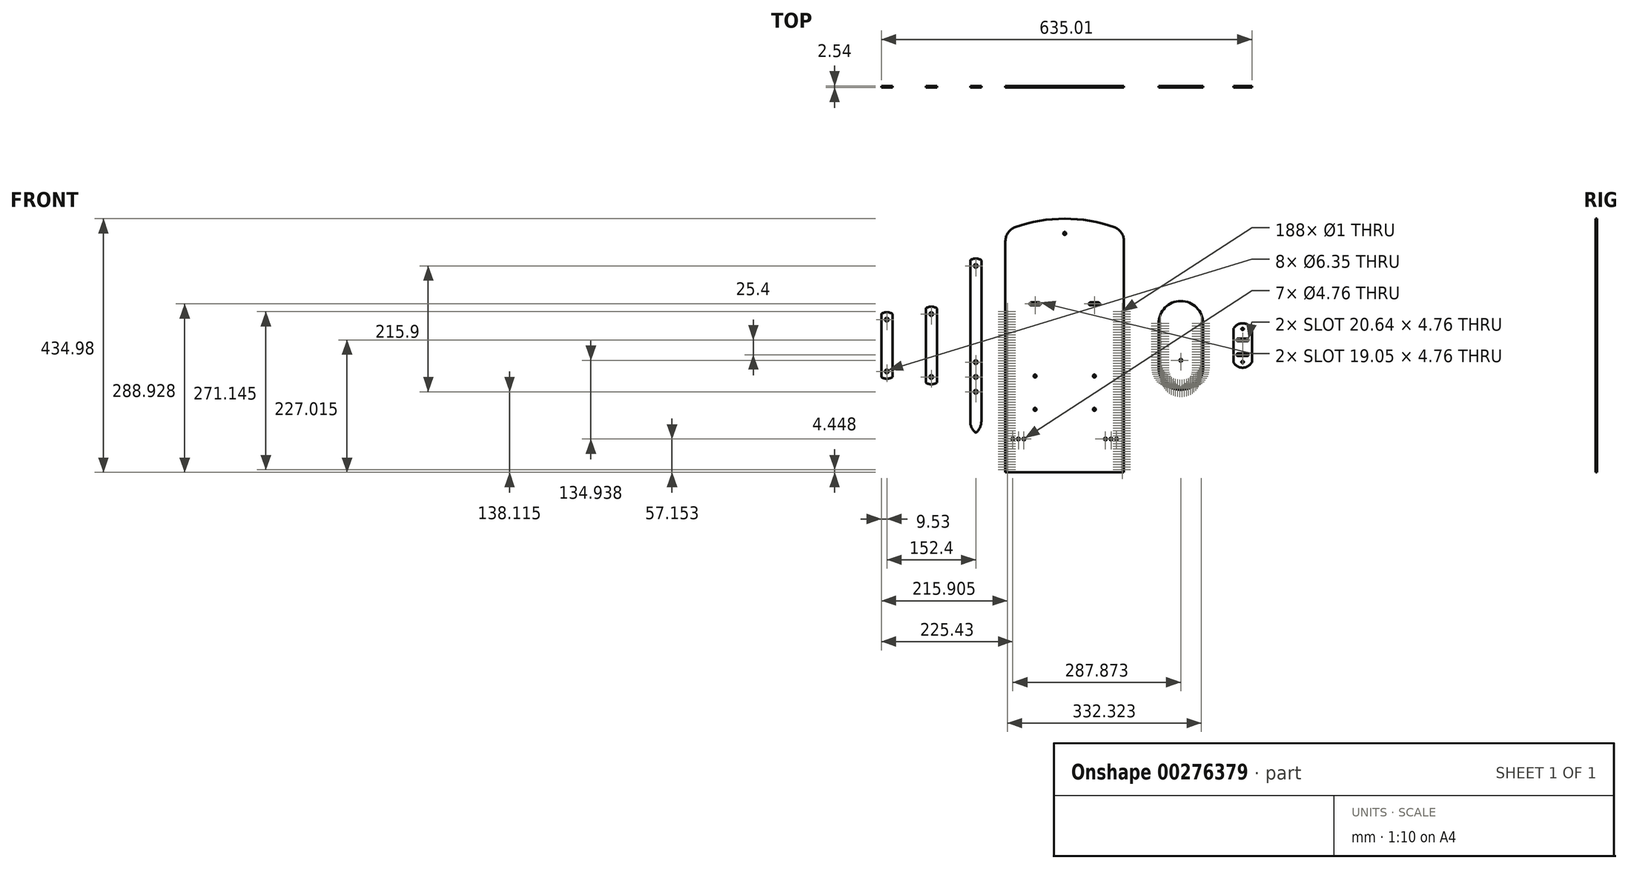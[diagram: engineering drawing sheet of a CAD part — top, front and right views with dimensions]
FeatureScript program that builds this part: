
annotation { "Feature Type Name" : "Feature", "Feature Type Description" : "" }
export const myFeature = defineFeature(function(context is Context, id is Id, definition is map)
    precondition{}
    {
        {
            var Q0;
            Q0=qCreatedBy(makeId("Front.planeOp"),FACE);
            var sketch = newSketch(context, id + "F0", { "sketchPlane" : qUnion([Q0])});
            skLineSegment(sketch, "E0.bottom", {"start": v(101.6, -217.49) * mm, "end": v(-101.6, -217.49) * mm, "construction": true});
            skLineSegment(sketch, "E0.top", {"start": v(101.6, 217.49) * mm, "end": v(-101.6, 217.49) * mm, "construction": true});
            skLineSegment(sketch, "E0.left", {"start": v(101.6, -217.49) * mm, "end": v(101.6, 217.49) * mm, "construction": true});
            skLineSegment(sketch, "E0.right", {"start": v(-101.6, -217.49) * mm, "end": v(-101.6, 217.49) * mm, "construction": true});
            skPoint(sketch, "E0.middle", {"position": v(0, 0) * mm});
            skArc(sketch, "E1", {"start": v(84.67, 202.96) * mm, "mid": v(0, 217.49) * mm, "end": v(-84.67, 202.96) * mm});
            skLineSegment(sketch, "E2", {"start": v(0, 0) * mm, "end": v(0, 217.49) * mm, "construction": true});
            skArc(sketch, "E3", {"start": v(-84.67, 202.96) * mm, "mid": v(-96.94, 193.68) * mm, "end": v(-101.6, 179.01) * mm});
            skPoint(sketch, "E4.orphan", {"position": v(-101.6, 196.28) * mm});
            skArc(sketch, "E5.MirrorCS", {"start": v(84.67, 202.96) * mm, "mid": v(96.94, 193.68) * mm, "end": v(101.6, 179.01) * mm});
            skPoint(sketch, "E6.orphan", {"position": v(101.6, 196.28) * mm});
            skLineSegment(sketch, "E7", {"start": v(-101.6, 179.01) * mm, "end": v(-101.6, -217.49) * mm});
            skLineSegment(sketch, "E8", {"start": v(101.6, -217.49) * mm, "end": v(-101.6, -217.49) * mm});
            skLineSegment(sketch, "E9", {"start": v(101.6, -217.49) * mm, "end": v(101.6, 179.01) * mm});
            skCircle(sketch, "E10", {"center": v(0, 192.09) * mm, "radius": 2.5 * mm});
            skLineSegment(sketch, "E11.bottom", {"start": v(-57.94, 69.06) * mm, "end": v(-43.66, 69.06) * mm});
            skLineSegment(sketch, "E11.top", {"start": v(-57.94, 73.82) * mm, "end": v(-43.66, 73.82) * mm});
            skLineSegment(sketch, "E11.left", {"start": v(-57.94, 69.06) * mm, "end": v(-57.94, 73.82) * mm, "construction": true});
            skLineSegment(sketch, "E11.right", {"start": v(-43.66, 69.06) * mm, "end": v(-43.66, 73.82) * mm, "construction": true});
            skPoint(sketch, "E11.middle", {"position": v(-50.8, 71.44) * mm});
            skArc(sketch, "E12", {"start": v(-43.66, 69.06) * mm, "mid": v(-41.27, 71.44) * mm, "end": v(-43.66, 73.82) * mm});
            skArc(sketch, "E13", {"start": v(-57.94, 73.82) * mm, "mid": v(-60.32, 71.44) * mm, "end": v(-57.94, 69.06) * mm});
            skLineSegment(sketch, "E14.MirrorCS", {"start": v(57.94, 73.82) * mm, "end": v(43.66, 73.82) * mm});
            skArc(sketch, "E15.MirrorCS", {"start": v(57.94, 73.82) * mm, "mid": v(60.32, 71.44) * mm, "end": v(57.94, 69.06) * mm});
            skLineSegment(sketch, "E16.MirrorCS", {"start": v(57.94, 69.06) * mm, "end": v(43.66, 69.06) * mm});
            skArc(sketch, "E17.MirrorCS", {"start": v(43.66, 69.06) * mm, "mid": v(41.27, 71.44) * mm, "end": v(43.66, 73.82) * mm});
            skLineSegment(sketch, "E18", {"start": v(-50.8, 71.44) * mm, "end": v(-50.8, -52.39) * mm, "construction": true});
            skCircle(sketch, "E19", {"center": v(-50.8, -52.39) * mm, "radius": 2.5 * mm});
            skCircle(sketch, "E20", {"center": v(-50.8, -109.54) * mm, "radius": 2.5 * mm});
            skCircle(sketch, "E21.MirrorC", {"center": v(50.8, -52.39) * mm, "radius": 2.5 * mm});
            skCircle(sketch, "E22.MirrorC", {"center": v(50.8, -109.54) * mm, "radius": 2.5 * mm});
            skLineSegment(sketch, "E23", {"start": v(-101.6, -160.34) * mm, "end": v(-57.15, -160.34) * mm, "construction": true});
            skCircle(sketch, "E24", {"center": v(-88.9, -160.34) * mm, "radius": 2.38 * mm});
            skCircle(sketch, "E25", {"center": v(-79.37, -160.34) * mm, "radius": 2.38 * mm});
            skCircle(sketch, "E26", {"center": v(-69.85, -160.34) * mm, "radius": 2.38 * mm});
            skCircle(sketch, "E27.MirrorC", {"center": v(88.9, -160.34) * mm, "radius": 2.38 * mm});
            skCircle(sketch, "E28.MirrorC", {"center": v(79.37, -160.34) * mm, "radius": 2.38 * mm});
            skCircle(sketch, "E29.MirrorC", {"center": v(69.85, -160.34) * mm, "radius": 2.38 * mm});
            skSolve(sketch);
        }
        {
            var Q0;
            Q0 = qSketchRegion(id + "F0", true);
            extrude(context, id + "F1", {"entities" : qUnion([Q0]), "depth" : 2.54 * mm});
        }
        {
            var Q0;
            Q0=qCreatedBy(makeId("Front.planeOp"),FACE);
            var sketch = newSketch(context, id + "F2", { "sketchPlane" : qUnion([Q0])});
            skLineSegment(sketch, "E30.bottom", {"start": v(237.07, -38.1) * mm, "end": v(160.87, -38.1) * mm, "construction": true});
            skLineSegment(sketch, "E30.top", {"start": v(237.07, 38.1) * mm, "end": v(160.87, 38.1) * mm, "construction": true});
            skLineSegment(sketch, "E30.left", {"start": v(237.07, -38.1) * mm, "end": v(237.07, 38.1) * mm});
            skLineSegment(sketch, "E30.right", {"start": v(160.87, -38.1) * mm, "end": v(160.87, 38.1) * mm});
            skPoint(sketch, "E30.middle", {"position": v(198.97, 0) * mm});
            skArc(sketch, "E31", {"start": v(237.07, 38.1) * mm, "mid": v(198.97, 76.2) * mm, "end": v(160.87, 38.1) * mm});
            skArc(sketch, "E32", {"start": v(160.87, -38.1) * mm, "mid": v(198.97, -76.2) * mm, "end": v(237.07, -38.1) * mm});
            skCircle(sketch, "E33", {"center": v(198.97, -25.4) * mm, "radius": 2.38 * mm});
            skSolve(sketch);
        }
        {
            var Q0;
            Q0 = qSketchRegion(id + "F2", true);
            extrude(context, id + "F3", {"entities" : qUnion([Q0]), "depth" : 2.54 * mm});
        }
        {
            var Q0;
            Q0=makeQuery(id+"F3.opExtrude","CAP_FACE",FACE,{"disambiguationData":[OSD([sQuery(id+"F2.wireOp",EDGE,"E30.left"),sQuery(id+"F2.wireOp",EDGE,"E30.right"),sQuery(id+"F2.wireOp",EDGE,"E31"),sQuery(id+"F2.wireOp",EDGE,"E32"),sQuery(id+"F2.wireOp",EDGE,"E33")])],"isStart":false});
            var sketch = newSketch(context, id + "F4", { "sketchPlane" : qUnion([Q0])});
            skArc(sketch, "E34.0", {"start": v(233.9, 38.1) * mm, "mid": v(198.97, 73.02) * mm, "end": v(164.05, 38.1) * mm, "construction": true});
            skLineSegment(sketch, "E34.1", {"start": v(233.9, -38.1) * mm, "end": v(233.9, 38.1) * mm, "construction": true});
            skArc(sketch, "E34.2", {"start": v(164.05, -38.1) * mm, "mid": v(198.97, -73.02) * mm, "end": v(233.9, -38.1) * mm, "construction": true});
            skLineSegment(sketch, "E34.3", {"start": v(164.05, -38.1) * mm, "end": v(164.05, 38.1) * mm, "construction": true});
            skCircle(sketch, "E35", {"center": v(233.9, 38.1) * mm, "radius": 0.5 * mm});
            skCircle(sketch, "E36.0.1.0", {"center": v(233.9, 33.62) * mm, "radius": 0.5 * mm});
            skCircle(sketch, "E36.0.2.0", {"center": v(233.9, 29.14) * mm, "radius": 0.5 * mm});
            skCircle(sketch, "E36.0.3.0", {"center": v(233.9, 24.65) * mm, "radius": 0.5 * mm});
            skCircle(sketch, "E36.0.4.0", {"center": v(233.9, 20.17) * mm, "radius": 0.5 * mm});
            skCircle(sketch, "E36.0.5.0", {"center": v(233.9, 15.69) * mm, "radius": 0.5 * mm});
            skCircle(sketch, "E36.0.6.0", {"center": v(233.9, 11.2) * mm, "radius": 0.5 * mm});
            skCircle(sketch, "E36.0.7.0", {"center": v(233.9, 6.72) * mm, "radius": 0.5 * mm});
            skCircle(sketch, "E36.0.8.0", {"center": v(233.9, 2.24) * mm, "radius": 0.5 * mm});
            skCircle(sketch, "E36.0.9.0", {"center": v(233.9, -2.24) * mm, "radius": 0.5 * mm});
            skCircle(sketch, "E36.0.10.0", {"center": v(233.9, -6.72) * mm, "radius": 0.5 * mm});
            skCircle(sketch, "E36.0.11.0", {"center": v(233.9, -11.2) * mm, "radius": 0.5 * mm});
            skCircle(sketch, "E36.0.12.0", {"center": v(233.9, -15.69) * mm, "radius": 0.5 * mm});
            skCircle(sketch, "E36.0.13.0", {"center": v(233.9, -20.17) * mm, "radius": 0.5 * mm});
            skCircle(sketch, "E36.0.14.0", {"center": v(233.9, -24.65) * mm, "radius": 0.5 * mm});
            skCircle(sketch, "E36.0.15.0", {"center": v(233.9, -29.14) * mm, "radius": 0.5 * mm});
            skCircle(sketch, "E36.0.16.0", {"center": v(233.9, -33.62) * mm, "radius": 0.5 * mm});
            skCircle(sketch, "E36.0.17.0", {"center": v(233.9, -38.1) * mm, "radius": 0.5 * mm});
            skLineSegment(sketch, "E36.direction1", {"start": v(233.9, 38.1) * mm, "end": v(259.3, 38.1) * mm, "construction": true});
            skLineSegment(sketch, "E36.direction2", {"start": v(233.9, 38.1) * mm, "end": v(233.9, 33.62) * mm, "construction": true});
            skCircle(sketch, "E37.1.0", {"center": v(233.7, -41.88) * mm, "radius": 0.5 * mm});
            skCircle(sketch, "E37.2.0", {"center": v(233.08, -45.6) * mm, "radius": 0.5 * mm});
            skCircle(sketch, "E37.3.0", {"center": v(232.07, -49.25) * mm, "radius": 0.5 * mm});
            skCircle(sketch, "E37.4.0", {"center": v(230.67, -52.76) * mm, "radius": 0.5 * mm});
            skCircle(sketch, "E37.5.0", {"center": v(228.9, -56.1) * mm, "radius": 0.5 * mm});
            skCircle(sketch, "E37.6.0", {"center": v(226.78, -59.24) * mm, "radius": 0.5 * mm});
            skCircle(sketch, "E37.7.0", {"center": v(224.33, -62.12) * mm, "radius": 0.5 * mm});
            skCircle(sketch, "E37.8.0", {"center": v(221.58, -64.72) * mm, "radius": 0.5 * mm});
            skCircle(sketch, "E37.9.0", {"center": v(218.57, -67) * mm, "radius": 0.5 * mm});
            skCircle(sketch, "E37.10.0", {"center": v(215.33, -68.96) * mm, "radius": 0.5 * mm});
            skCircle(sketch, "E37.11.0", {"center": v(211.9, -70.54) * mm, "radius": 0.5 * mm});
            skCircle(sketch, "E37.12.0", {"center": v(208.32, -71.75) * mm, "radius": 0.5 * mm});
            skCircle(sketch, "E37.13.0", {"center": v(204.62, -72.56) * mm, "radius": 0.5 * mm});
            skCircle(sketch, "E37.14.0", {"center": v(200.86, -72.97) * mm, "radius": 0.5 * mm});
            skCircle(sketch, "E37.15.0", {"center": v(197.08, -72.97) * mm, "radius": 0.5 * mm});
            skCircle(sketch, "E37.16.0", {"center": v(193.32, -72.56) * mm, "radius": 0.5 * mm});
            skCircle(sketch, "E37.17.0", {"center": v(189.63, -71.75) * mm, "radius": 0.5 * mm});
            skCircle(sketch, "E37.18.0", {"center": v(186.05, -70.54) * mm, "radius": 0.5 * mm});
            skCircle(sketch, "E37.19.0", {"center": v(182.61, -68.96) * mm, "radius": 0.5 * mm});
            skCircle(sketch, "E37.20.0", {"center": v(179.37, -67) * mm, "radius": 0.5 * mm});
            skCircle(sketch, "E37.21.0", {"center": v(176.36, -64.72) * mm, "radius": 0.5 * mm});
            skCircle(sketch, "E37.22.0", {"center": v(173.62, -62.12) * mm, "radius": 0.5 * mm});
            skCircle(sketch, "E37.23.0", {"center": v(171.17, -59.24) * mm, "radius": 0.5 * mm});
            skCircle(sketch, "E37.24.0", {"center": v(169.05, -56.1) * mm, "radius": 0.5 * mm});
            skCircle(sketch, "E37.25.0", {"center": v(167.28, -52.76) * mm, "radius": 0.5 * mm});
            skCircle(sketch, "E37.26.0", {"center": v(165.88, -49.25) * mm, "radius": 0.5 * mm});
            skCircle(sketch, "E37.27.0", {"center": v(164.86, -45.6) * mm, "radius": 0.5 * mm});
            skCircle(sketch, "E37.28.0", {"center": v(164.25, -41.88) * mm, "radius": 0.5 * mm});
            skCircle(sketch, "E37.29.0", {"center": v(164.05, -38.1) * mm, "radius": 0.5 * mm});
            skLineSegment(sketch, "E37.anchor1", {"start": v(198.97, -38.1) * mm, "end": v(233.9, -38.1) * mm, "construction": true});
            skLineSegment(sketch, "E37.anchor2", {"start": v(198.97, -38.1) * mm, "end": v(164.05, -38.1) * mm, "construction": true});
            skLineSegment(sketch, "E38", {"start": v(198.97, 38.1) * mm, "end": v(198.97, -38.1) * mm, "construction": true});
            skCircle(sketch, "E39.MirrorC", {"center": v(164.05, 38.1) * mm, "radius": 0.5 * mm});
            skCircle(sketch, "E40.MirrorC", {"center": v(164.05, 33.62) * mm, "radius": 0.5 * mm});
            skCircle(sketch, "E41.MirrorC", {"center": v(164.05, -20.17) * mm, "radius": 0.5 * mm});
            skCircle(sketch, "E42.MirrorC", {"center": v(164.05, -24.65) * mm, "radius": 0.5 * mm});
            skCircle(sketch, "E43.MirrorC", {"center": v(164.05, -29.14) * mm, "radius": 0.5 * mm});
            skCircle(sketch, "E44.MirrorC", {"center": v(164.05, -2.24) * mm, "radius": 0.5 * mm});
            skCircle(sketch, "E45.MirrorC", {"center": v(164.05, -6.72) * mm, "radius": 0.5 * mm});
            skCircle(sketch, "E46.MirrorC", {"center": v(164.05, -11.2) * mm, "radius": 0.5 * mm});
            skCircle(sketch, "E47.MirrorC", {"center": v(164.05, -15.69) * mm, "radius": 0.5 * mm});
            skCircle(sketch, "E48.MirrorC", {"center": v(164.05, 29.14) * mm, "radius": 0.5 * mm});
            skLineSegment(sketch, "E49.MirrorCS", {"start": v(164.05, 38.1) * mm, "end": v(164.05, 33.62) * mm, "construction": true});
            skCircle(sketch, "E50.MirrorC", {"center": v(164.05, 24.65) * mm, "radius": 0.5 * mm});
            skCircle(sketch, "E51.MirrorC", {"center": v(164.05, 11.2) * mm, "radius": 0.5 * mm});
            skCircle(sketch, "E52.MirrorC", {"center": v(164.05, -33.62) * mm, "radius": 0.5 * mm});
            skCircle(sketch, "E53.MirrorC", {"center": v(164.05, 6.72) * mm, "radius": 0.5 * mm});
            skCircle(sketch, "E54.MirrorC", {"center": v(164.05, 2.24) * mm, "radius": 0.5 * mm});
            skCircle(sketch, "E55.MirrorC", {"center": v(164.05, 20.17) * mm, "radius": 0.5 * mm});
            skCircle(sketch, "E56.MirrorC", {"center": v(164.05, 15.69) * mm, "radius": 0.5 * mm});
            skSolve(sketch);
        }
        {
            var Q0;
            Q0 = qSketchRegion(id + "F4", true);
            extrude(context, id + "F5", {"entities" : qUnion([Q0]), "operationType" : NewBodyOperationType.REMOVE, "endBound" : BoundingType.THROUGH_ALL, "oppositeDirection" : true, "depth" : 25.4 * mm});
        }
        {
            var Q0;
            Q0=makeQuery(id+"F1.opExtrude","CAP_FACE",FACE,{"disambiguationData":[OSD([sQuery(id+"F0.wireOp",EDGE,"E1"),sQuery(id+"F0.wireOp",EDGE,"E3"),sQuery(id+"F0.wireOp",EDGE,"E5.MirrorCS"),sQuery(id+"F0.wireOp",EDGE,"E7"),sQuery(id+"F0.wireOp",EDGE,"E8"),sQuery(id+"F0.wireOp",EDGE,"E9"),sQuery(id+"F0.wireOp",EDGE,"E10"),sQuery(id+"F0.wireOp",EDGE,"E11.bottom"),sQuery(id+"F0.wireOp",EDGE,"E11.top"),sQuery(id+"F0.wireOp",EDGE,"E12"),sQuery(id+"F0.wireOp",EDGE,"E13"),sQuery(id+"F0.wireOp",EDGE,"E14.MirrorCS"),sQuery(id+"F0.wireOp",EDGE,"E15.MirrorCS"),sQuery(id+"F0.wireOp",EDGE,"E16.MirrorCS"),sQuery(id+"F0.wireOp",EDGE,"E17.MirrorCS"),sQuery(id+"F0.wireOp",EDGE,"E19"),sQuery(id+"F0.wireOp",EDGE,"E20"),sQuery(id+"F0.wireOp",EDGE,"E21.MirrorC"),sQuery(id+"F0.wireOp",EDGE,"E22.MirrorC"),sQuery(id+"F0.wireOp",EDGE,"E24"),sQuery(id+"F0.wireOp",EDGE,"E25"),sQuery(id+"F0.wireOp",EDGE,"E26"),sQuery(id+"F0.wireOp",EDGE,"E27.MirrorC"),sQuery(id+"F0.wireOp",EDGE,"E28.MirrorC"),sQuery(id+"F0.wireOp",EDGE,"E29.MirrorC")])],"isStart":false});
            var sketch = newSketch(context, id + "F6", { "sketchPlane" : qUnion([Q0])});
            skLineSegment(sketch, "E57", {"start": v(98.43, -83.45) * mm, "end": v(98.43, -217.49) * mm, "construction": true});
            skCircle(sketch, "E58", {"center": v(98.43, -213.04) * mm, "radius": 0.5 * mm});
            skCircle(sketch, "E59.0.1.0", {"center": v(98.43, -208.6) * mm, "radius": 0.5 * mm});
            skCircle(sketch, "E59.0.2.0", {"center": v(98.43, -204.15) * mm, "radius": 0.5 * mm});
            skCircle(sketch, "E59.0.3.0", {"center": v(98.43, -199.7) * mm, "radius": 0.5 * mm});
            skCircle(sketch, "E59.0.4.0", {"center": v(98.43, -195.26) * mm, "radius": 0.5 * mm});
            skCircle(sketch, "E59.0.5.0", {"center": v(98.43, -190.82) * mm, "radius": 0.5 * mm});
            skCircle(sketch, "E59.0.6.0", {"center": v(98.43, -186.37) * mm, "radius": 0.5 * mm});
            skCircle(sketch, "E59.0.7.0", {"center": v(98.43, -181.93) * mm, "radius": 0.5 * mm});
            skCircle(sketch, "E59.0.8.0", {"center": v(98.43, -177.48) * mm, "radius": 0.5 * mm});
            skCircle(sketch, "E59.0.9.0", {"center": v(98.43, -173.04) * mm, "radius": 0.5 * mm});
            skCircle(sketch, "E59.0.10.0", {"center": v(98.43, -168.6) * mm, "radius": 0.5 * mm});
            skCircle(sketch, "E59.0.11.0", {"center": v(98.43, -164.15) * mm, "radius": 0.5 * mm});
            skCircle(sketch, "E59.0.12.0", {"center": v(98.43, -159.7) * mm, "radius": 0.5 * mm});
            skCircle(sketch, "E59.0.13.0", {"center": v(98.43, -155.26) * mm, "radius": 0.5 * mm});
            skCircle(sketch, "E59.0.14.0", {"center": v(98.43, -150.81) * mm, "radius": 0.5 * mm});
            skCircle(sketch, "E59.0.15.0", {"center": v(98.43, -146.37) * mm, "radius": 0.5 * mm});
            skCircle(sketch, "E59.0.16.0", {"center": v(98.43, -141.92) * mm, "radius": 0.5 * mm});
            skCircle(sketch, "E59.0.17.0", {"center": v(98.43, -137.48) * mm, "radius": 0.5 * mm});
            skCircle(sketch, "E59.0.18.0", {"center": v(98.43, -133.03) * mm, "radius": 0.5 * mm});
            skCircle(sketch, "E59.0.19.0", {"center": v(98.43, -128.59) * mm, "radius": 0.5 * mm});
            skCircle(sketch, "E59.0.20.0", {"center": v(98.43, -124.14) * mm, "radius": 0.5 * mm});
            skCircle(sketch, "E59.0.21.0", {"center": v(98.43, -119.7) * mm, "radius": 0.5 * mm});
            skCircle(sketch, "E59.0.22.0", {"center": v(98.43, -115.25) * mm, "radius": 0.5 * mm});
            skCircle(sketch, "E59.0.23.0", {"center": v(98.43, -110.8) * mm, "radius": 0.5 * mm});
            skCircle(sketch, "E59.0.24.0", {"center": v(98.43, -106.36) * mm, "radius": 0.5 * mm});
            skCircle(sketch, "E59.0.25.0", {"center": v(98.43, -101.92) * mm, "radius": 0.5 * mm});
            skCircle(sketch, "E59.0.26.0", {"center": v(98.43, -97.47) * mm, "radius": 0.5 * mm});
            skCircle(sketch, "E59.0.27.0", {"center": v(98.43, -93.03) * mm, "radius": 0.5 * mm});
            skCircle(sketch, "E59.0.28.0", {"center": v(98.43, -88.58) * mm, "radius": 0.5 * mm});
            skCircle(sketch, "E59.0.29.0", {"center": v(98.43, -84.14) * mm, "radius": 0.5 * mm});
            skCircle(sketch, "E59.0.30.0", {"center": v(98.43, -79.7) * mm, "radius": 0.5 * mm});
            skCircle(sketch, "E59.0.31.0", {"center": v(98.43, -75.25) * mm, "radius": 0.5 * mm});
            skCircle(sketch, "E59.0.32.0", {"center": v(98.43, -70.8) * mm, "radius": 0.5 * mm});
            skCircle(sketch, "E59.0.33.0", {"center": v(98.43, -66.36) * mm, "radius": 0.5 * mm});
            skCircle(sketch, "E59.0.34.0", {"center": v(98.43, -61.91) * mm, "radius": 0.5 * mm});
            skCircle(sketch, "E59.0.35.0", {"center": v(98.43, -57.47) * mm, "radius": 0.5 * mm});
            skCircle(sketch, "E59.0.36.0", {"center": v(98.43, -53.02) * mm, "radius": 0.5 * mm});
            skCircle(sketch, "E59.0.37.0", {"center": v(98.43, -48.58) * mm, "radius": 0.5 * mm});
            skCircle(sketch, "E59.0.38.0", {"center": v(98.43, -44.13) * mm, "radius": 0.5 * mm});
            skCircle(sketch, "E59.0.39.0", {"center": v(98.43, -39.69) * mm, "radius": 0.5 * mm});
            skCircle(sketch, "E59.0.40.0", {"center": v(98.43, -35.24) * mm, "radius": 0.5 * mm});
            skCircle(sketch, "E59.0.41.0", {"center": v(98.43, -30.8) * mm, "radius": 0.5 * mm});
            skCircle(sketch, "E59.0.42.0", {"center": v(98.43, -26.35) * mm, "radius": 0.5 * mm});
            skCircle(sketch, "E59.0.43.0", {"center": v(98.43, -21.9) * mm, "radius": 0.5 * mm});
            skCircle(sketch, "E59.0.44.0", {"center": v(98.43, -17.46) * mm, "radius": 0.5 * mm});
            skCircle(sketch, "E59.0.45.0", {"center": v(98.43, -13.02) * mm, "radius": 0.5 * mm});
            skCircle(sketch, "E59.0.46.0", {"center": v(98.43, -8.57) * mm, "radius": 0.5 * mm});
            skCircle(sketch, "E59.0.47.0", {"center": v(98.43, -4.13) * mm, "radius": 0.5 * mm});
            skCircle(sketch, "E59.0.48.0", {"center": v(98.43, 0.32) * mm, "radius": 0.5 * mm});
            skCircle(sketch, "E59.0.49.0", {"center": v(98.43, 4.76) * mm, "radius": 0.5 * mm});
            skCircle(sketch, "E59.0.50.0", {"center": v(98.43, 9.2) * mm, "radius": 0.5 * mm});
            skCircle(sketch, "E59.0.51.0", {"center": v(98.43, 13.65) * mm, "radius": 0.5 * mm});
            skCircle(sketch, "E59.0.52.0", {"center": v(98.43, 18.1) * mm, "radius": 0.5 * mm});
            skCircle(sketch, "E59.0.53.0", {"center": v(98.43, 22.54) * mm, "radius": 0.5 * mm});
            skCircle(sketch, "E59.0.54.0", {"center": v(98.43, 26.99) * mm, "radius": 0.5 * mm});
            skCircle(sketch, "E59.0.55.0", {"center": v(98.43, 31.43) * mm, "radius": 0.5 * mm});
            skCircle(sketch, "E59.0.56.0", {"center": v(98.43, 35.88) * mm, "radius": 0.5 * mm});
            skCircle(sketch, "E59.0.57.0", {"center": v(98.43, 40.32) * mm, "radius": 0.5 * mm});
            skCircle(sketch, "E59.0.58.0", {"center": v(98.43, 44.77) * mm, "radius": 0.5 * mm});
            skCircle(sketch, "E59.0.59.0", {"center": v(98.43, 49.21) * mm, "radius": 0.5 * mm});
            skCircle(sketch, "E59.0.60.0", {"center": v(98.43, 53.66) * mm, "radius": 0.5 * mm});
            skCircle(sketch, "E59.0.61.0", {"center": v(98.43, 58.1) * mm, "radius": 0.5 * mm});
            skLineSegment(sketch, "E59.direction1", {"start": v(98.43, -213.04) * mm, "end": v(123.83, -213.04) * mm, "construction": true});
            skLineSegment(sketch, "E59.direction2", {"start": v(98.43, -213.04) * mm, "end": v(98.43, -208.6) * mm, "construction": true});
            skCircle(sketch, "E60.MirrorC", {"center": v(-98.43, -213.04) * mm, "radius": 0.5 * mm});
            skLineSegment(sketch, "E61.MirrorCS", {"start": v(-98.43, -213.04) * mm, "end": v(-98.43, -208.6) * mm, "construction": true});
            skCircle(sketch, "E62.MirrorC", {"center": v(-98.43, -204.15) * mm, "radius": 0.5 * mm});
            skCircle(sketch, "E63.MirrorC", {"center": v(-98.43, -208.6) * mm, "radius": 0.5 * mm});
            skCircle(sketch, "E64.MirrorC", {"center": v(-98.43, -164.15) * mm, "radius": 0.5 * mm});
            skCircle(sketch, "E65.MirrorC", {"center": v(-98.43, -168.6) * mm, "radius": 0.5 * mm});
            skCircle(sketch, "E66.MirrorC", {"center": v(-98.43, -173.04) * mm, "radius": 0.5 * mm});
            skCircle(sketch, "E67.MirrorC", {"center": v(-98.43, -177.48) * mm, "radius": 0.5 * mm});
            skCircle(sketch, "E68.MirrorC", {"center": v(-98.43, -181.93) * mm, "radius": 0.5 * mm});
            skCircle(sketch, "E69.MirrorC", {"center": v(-98.43, -186.37) * mm, "radius": 0.5 * mm});
            skCircle(sketch, "E70.MirrorC", {"center": v(-98.43, -190.82) * mm, "radius": 0.5 * mm});
            skCircle(sketch, "E71.MirrorC", {"center": v(-98.43, -195.26) * mm, "radius": 0.5 * mm});
            skCircle(sketch, "E72.MirrorC", {"center": v(-98.43, -199.7) * mm, "radius": 0.5 * mm});
            skCircle(sketch, "E73.MirrorC", {"center": v(-98.43, -159.7) * mm, "radius": 0.5 * mm});
            skCircle(sketch, "E74.MirrorC", {"center": v(-98.43, -79.7) * mm, "radius": 0.5 * mm});
            skCircle(sketch, "E75.MirrorC", {"center": v(-98.43, -84.14) * mm, "radius": 0.5 * mm});
            skCircle(sketch, "E76.MirrorC", {"center": v(-98.43, -21.9) * mm, "radius": 0.5 * mm});
            skCircle(sketch, "E77.MirrorC", {"center": v(-98.43, -93.03) * mm, "radius": 0.5 * mm});
            skCircle(sketch, "E78.MirrorC", {"center": v(-98.43, -57.47) * mm, "radius": 0.5 * mm});
            skCircle(sketch, "E79.MirrorC", {"center": v(-98.43, -88.58) * mm, "radius": 0.5 * mm});
            skCircle(sketch, "E80.MirrorC", {"center": v(-98.43, -26.35) * mm, "radius": 0.5 * mm});
            skCircle(sketch, "E81.MirrorC", {"center": v(-98.43, 44.77) * mm, "radius": 0.5 * mm});
            skCircle(sketch, "E82.MirrorC", {"center": v(-98.43, -97.47) * mm, "radius": 0.5 * mm});
            skCircle(sketch, "E83.MirrorC", {"center": v(-98.43, -133.03) * mm, "radius": 0.5 * mm});
            skCircle(sketch, "E84.MirrorC", {"center": v(-98.43, -61.91) * mm, "radius": 0.5 * mm});
            skCircle(sketch, "E85.MirrorC", {"center": v(-98.43, 9.2) * mm, "radius": 0.5 * mm});
            skCircle(sketch, "E86.MirrorC", {"center": v(-98.43, -30.8) * mm, "radius": 0.5 * mm});
            skCircle(sketch, "E87.MirrorC", {"center": v(-98.43, 40.32) * mm, "radius": 0.5 * mm});
            skCircle(sketch, "E88.MirrorC", {"center": v(-98.43, -101.92) * mm, "radius": 0.5 * mm});
            skCircle(sketch, "E89.MirrorC", {"center": v(-98.43, -137.48) * mm, "radius": 0.5 * mm});
            skCircle(sketch, "E90.MirrorC", {"center": v(-98.43, -66.36) * mm, "radius": 0.5 * mm});
            skCircle(sketch, "E91.MirrorC", {"center": v(-98.43, 4.76) * mm, "radius": 0.5 * mm});
            skCircle(sketch, "E92.MirrorC", {"center": v(-98.43, 35.88) * mm, "radius": 0.5 * mm});
            skCircle(sketch, "E93.MirrorC", {"center": v(-98.43, -106.36) * mm, "radius": 0.5 * mm});
            skCircle(sketch, "E94.MirrorC", {"center": v(-98.43, -39.69) * mm, "radius": 0.5 * mm});
            skCircle(sketch, "E95.MirrorC", {"center": v(-98.43, 31.43) * mm, "radius": 0.5 * mm});
            skCircle(sketch, "E96.MirrorC", {"center": v(-98.43, -110.8) * mm, "radius": 0.5 * mm});
            skCircle(sketch, "E97.MirrorC", {"center": v(-98.43, -141.92) * mm, "radius": 0.5 * mm});
            skCircle(sketch, "E98.MirrorC", {"center": v(-98.43, 0.32) * mm, "radius": 0.5 * mm});
            skCircle(sketch, "E99.MirrorC", {"center": v(-98.43, -44.13) * mm, "radius": 0.5 * mm});
            skCircle(sketch, "E100.MirrorC", {"center": v(-98.43, 26.99) * mm, "radius": 0.5 * mm});
            skCircle(sketch, "E101.MirrorC", {"center": v(-98.43, -115.25) * mm, "radius": 0.5 * mm});
            skLineSegment(sketch, "E102.MirrorCS", {"start": v(-98.43, -83.45) * mm, "end": v(-98.43, -217.49) * mm, "construction": true});
            skCircle(sketch, "E103.MirrorC", {"center": v(-98.43, -150.81) * mm, "radius": 0.5 * mm});
            skCircle(sketch, "E104.MirrorC", {"center": v(-98.43, -155.26) * mm, "radius": 0.5 * mm});
            skLineSegment(sketch, "E105.MirrorCS", {"start": v(-98.43, -213.04) * mm, "end": v(-123.83, -213.04) * mm, "construction": true});
            skCircle(sketch, "E106.MirrorC", {"center": v(-98.43, -119.7) * mm, "radius": 0.5 * mm});
            skCircle(sketch, "E107.MirrorC", {"center": v(-98.43, -48.58) * mm, "radius": 0.5 * mm});
            skCircle(sketch, "E108.MirrorC", {"center": v(-98.43, 22.54) * mm, "radius": 0.5 * mm});
            skCircle(sketch, "E109.MirrorC", {"center": v(-98.43, -8.57) * mm, "radius": 0.5 * mm});
            skCircle(sketch, "E110.MirrorC", {"center": v(-98.43, 58.1) * mm, "radius": 0.5 * mm});
            skCircle(sketch, "E111.MirrorC", {"center": v(-98.43, -124.14) * mm, "radius": 0.5 * mm});
            skCircle(sketch, "E112.MirrorC", {"center": v(-98.43, -53.02) * mm, "radius": 0.5 * mm});
            skCircle(sketch, "E113.MirrorC", {"center": v(-98.43, -13.02) * mm, "radius": 0.5 * mm});
            skCircle(sketch, "E114.MirrorC", {"center": v(-98.43, 18.1) * mm, "radius": 0.5 * mm});
            skCircle(sketch, "E115.MirrorC", {"center": v(-98.43, 49.21) * mm, "radius": 0.5 * mm});
            skCircle(sketch, "E116.MirrorC", {"center": v(-98.43, 53.66) * mm, "radius": 0.5 * mm});
            skCircle(sketch, "E117.MirrorC", {"center": v(-98.43, -128.59) * mm, "radius": 0.5 * mm});
            skCircle(sketch, "E118.MirrorC", {"center": v(-98.43, -17.46) * mm, "radius": 0.5 * mm});
            skCircle(sketch, "E119.MirrorC", {"center": v(-98.43, 13.65) * mm, "radius": 0.5 * mm});
            skCircle(sketch, "E120.MirrorC", {"center": v(-98.43, -35.24) * mm, "radius": 0.5 * mm});
            skCircle(sketch, "E121.MirrorC", {"center": v(-98.43, -70.8) * mm, "radius": 0.5 * mm});
            skCircle(sketch, "E122.MirrorC", {"center": v(-98.43, -146.37) * mm, "radius": 0.5 * mm});
            skCircle(sketch, "E123.MirrorC", {"center": v(-98.43, -75.25) * mm, "radius": 0.5 * mm});
            skCircle(sketch, "E124.MirrorC", {"center": v(-98.43, -4.13) * mm, "radius": 0.5 * mm});
            skSolve(sketch);
        }
        {
            var Q0;
            Q0 = qSketchRegion(id + "F6", true);
            extrude(context, id + "F7", {"entities" : qUnion([Q0]), "operationType" : NewBodyOperationType.REMOVE, "endBound" : BoundingType.THROUGH_ALL, "oppositeDirection" : true, "depth" : 25.4 * mm});
        }
        {
            var Q0;
            Q0=qCreatedBy(makeId("Front.planeOp"),FACE);
            var sketch = newSketch(context, id + "F8", { "sketchPlane" : qUnion([Q0])});
            skLineSegment(sketch, "E125.bottom", {"start": v(-142.87, -149.23) * mm, "end": v(-161.92, -149.23) * mm, "construction": true});
            skLineSegment(sketch, "E125.top", {"start": v(-142.88, 149.23) * mm, "end": v(-161.93, 149.23) * mm, "construction": true});
            skLineSegment(sketch, "E125.left", {"start": v(-142.88, -149.23) * mm, "end": v(-142.88, 146.05) * mm});
            skLineSegment(sketch, "E125.right", {"start": v(-161.93, -149.23) * mm, "end": v(-161.93, 146.05) * mm});
            skPoint(sketch, "E125.middle", {"position": v(-152.4, 0) * mm});
            skLineSegment(sketch, "E126.bottom", {"start": v(-295.28, -57.15) * mm, "end": v(-314.33, -57.15) * mm, "construction": true});
            skLineSegment(sketch, "E126.top", {"start": v(-295.28, 57.15) * mm, "end": v(-314.33, 57.15) * mm, "construction": true});
            skLineSegment(sketch, "E126.left", {"start": v(-295.28, -57.15) * mm, "end": v(-295.28, 53.98) * mm});
            skLineSegment(sketch, "E126.right", {"start": v(-314.33, -57.15) * mm, "end": v(-314.33, 53.98) * mm});
            skPoint(sketch, "E126.middle", {"position": v(-304.8, 0) * mm});
            skLineSegment(sketch, "E127.bottom", {"start": v(-219.08, -66.68) * mm, "end": v(-238.13, -66.68) * mm, "construction": true});
            skLineSegment(sketch, "E127.top", {"start": v(-219.07, 66.68) * mm, "end": v(-238.13, 66.68) * mm, "construction": true});
            skLineSegment(sketch, "E127.left", {"start": v(-219.07, -66.68) * mm, "end": v(-219.07, 63.5) * mm});
            skLineSegment(sketch, "E127.right", {"start": v(-238.13, -66.67) * mm, "end": v(-238.13, 63.5) * mm});
            skPoint(sketch, "E127.middle", {"position": v(-228.6, 0) * mm});
            skArc(sketch, "E128", {"start": v(-295.28, 53.98) * mm, "mid": v(-304.8, 57.15) * mm, "end": v(-314.32, 53.98) * mm});
            skLineSegment(sketch, "E129", {"start": v(-304.8, 0) * mm, "end": v(-304.8, 39.15) * mm, "construction": true});
            skLineSegment(sketch, "E130", {"start": v(-304.8, 0) * mm, "end": v(-152.4, 0) * mm, "construction": true});
            skArc(sketch, "E131", {"start": v(-219.07, 63.5) * mm, "mid": v(-228.6, 66.68) * mm, "end": v(-238.13, 63.5) * mm});
            skArc(sketch, "E132", {"start": v(-142.88, 146.05) * mm, "mid": v(-152.4, 149.22) * mm, "end": v(-161.93, 146.05) * mm});
            skLineSegment(sketch, "E133", {"start": v(-228.6, 0) * mm, "end": v(-228.6, 61.41) * mm, "construction": true});
            skLineSegment(sketch, "E134", {"start": v(-152.4, 0) * mm, "end": v(-152.4, 112.97) * mm, "construction": true});
            skArc(sketch, "E135.MirrorCS", {"start": v(-295.28, -53.97) * mm, "mid": v(-304.8, -57.15) * mm, "end": v(-314.33, -53.97) * mm});
            skArc(sketch, "E136.MirrorCS", {"start": v(-219.07, -63.5) * mm, "mid": v(-228.6, -66.67) * mm, "end": v(-238.13, -63.5) * mm});
            skPoint(sketch, "E137.visualSharp", {"position": v(-152.4, -149.23) * mm});
            skCircle(sketch, "E138", {"center": v(-152.4, -147.64) * mm, "radius": 1.59 * mm, "construction": true});
            skLineSegment(sketch, "E139", {"start": v(-150.95, -148.28) * mm, "end": v(-142.87, -130.18) * mm, "construction": true});
            skLineSegment(sketch, "E140", {"start": v(-153.85, -148.28) * mm, "end": v(-161.93, -130.18) * mm, "construction": true});
            skLineSegment(sketch, "E141", {"start": v(-161.93, -130.18) * mm, "end": v(-142.88, -130.18) * mm, "construction": true});
            skArc(sketch, "E142", {"start": v(-151.34, -148.82) * mm, "mid": v(-145.15, -140.39) * mm, "end": v(-142.88, -130.18) * mm});
            skArc(sketch, "E143", {"start": v(-161.93, -130.18) * mm, "mid": v(-159.65, -140.39) * mm, "end": v(-153.46, -148.82) * mm});
            skArc(sketch, "E144", {"start": v(-153.46, -148.82) * mm, "mid": v(-152.4, -149.23) * mm, "end": v(-151.34, -148.82) * mm});
            skCircle(sketch, "E145", {"center": v(-152.4, -79.38) * mm, "radius": 3.18 * mm});
            skCircle(sketch, "E146.0.1.0", {"center": v(-152.4, -53.98) * mm, "radius": 3.18 * mm});
            skCircle(sketch, "E146.0.2.0", {"center": v(-152.4, -28.58) * mm, "radius": 3.18 * mm});
            skLineSegment(sketch, "E146.direction1", {"start": v(-152.4, -79.38) * mm, "end": v(-127, -79.38) * mm, "construction": true});
            skLineSegment(sketch, "E146.direction2", {"start": v(-152.4, -79.38) * mm, "end": v(-152.4, -53.98) * mm, "construction": true});
            skCircle(sketch, "E147", {"center": v(-304.8, 44.45) * mm, "radius": 3.18 * mm});
            skCircle(sketch, "E148", {"center": v(-228.6, 53.98) * mm, "radius": 3.18 * mm});
            skCircle(sketch, "E149", {"center": v(-152.4, 136.53) * mm, "radius": 3.18 * mm});
            skCircle(sketch, "E150.MirrorC", {"center": v(-304.8, -44.45) * mm, "radius": 3.18 * mm});
            skCircle(sketch, "E151.MirrorC", {"center": v(-228.6, -53.97) * mm, "radius": 3.18 * mm});
            skSolve(sketch);
        }
        {
            var Q0;
            Q0 = qSketchRegion(id + "F8", true);
            extrude(context, id + "F9", {"entities" : qUnion([Q0]), "depth" : 2.54 * mm});
        }
        {
            var Q0;
            Q0=qCreatedBy(makeId("Front.planeOp"),FACE);
            var sketch = newSketch(context, id + "F10", { "sketchPlane" : qUnion([Q0])});
            skLineSegment(sketch, "E152.bottom", {"start": v(320.68, -38.1) * mm, "end": v(288.93, -38.1) * mm, "construction": true});
            skLineSegment(sketch, "E152.top", {"start": v(320.68, 38.1) * mm, "end": v(288.93, 38.1) * mm, "construction": true});
            skLineSegment(sketch, "E152.left", {"start": v(320.68, -28.33) * mm, "end": v(320.68, 28.33) * mm});
            skLineSegment(sketch, "E152.right", {"start": v(288.93, -28.33) * mm, "end": v(288.93, 28.33) * mm});
            skPoint(sketch, "E152.middle", {"position": v(304.8, 0) * mm});
            skArc(sketch, "E153", {"start": v(320.68, 28.33) * mm, "mid": v(304.8, 38.1) * mm, "end": v(288.93, 28.33) * mm});
            skLineSegment(sketch, "E154", {"start": v(304.8, 0) * mm, "end": v(304.8, 19.05) * mm, "construction": true});
            skLineSegment(sketch, "E155", {"start": v(304.8, 0) * mm, "end": v(320.68, 0) * mm, "construction": true});
            skArc(sketch, "E156.MirrorCS", {"start": v(320.68, -28.33) * mm, "mid": v(304.8, -38.1) * mm, "end": v(288.93, -28.33) * mm});
            skLineSegment(sketch, "E157.bottom", {"start": v(312.74, -18.26) * mm, "end": v(296.86, -18.26) * mm});
            skLineSegment(sketch, "E157.top", {"start": v(312.74, -13.5) * mm, "end": v(296.86, -13.5) * mm});
            skLineSegment(sketch, "E157.left", {"start": v(315.12, -15.88) * mm, "end": v(315.12, -15.88) * mm});
            skLineSegment(sketch, "E157.right", {"start": v(294.48, -15.88) * mm, "end": v(294.48, -15.88) * mm});
            skPoint(sketch, "E157.middle", {"position": v(304.8, -15.87) * mm});
            skLineSegment(sketch, "E158.bottom", {"start": v(312.74, 7.14) * mm, "end": v(296.86, 7.14) * mm});
            skLineSegment(sketch, "E158.top", {"start": v(312.74, 11.9) * mm, "end": v(296.86, 11.9) * mm});
            skLineSegment(sketch, "E158.left", {"start": v(315.12, 9.53) * mm, "end": v(315.12, 9.53) * mm});
            skLineSegment(sketch, "E158.right", {"start": v(294.48, 9.53) * mm, "end": v(294.48, 9.53) * mm});
            skPoint(sketch, "E158.middle", {"position": v(304.8, 9.53) * mm});
            skLineSegment(sketch, "E159", {"start": v(288.93, 28.33) * mm, "end": v(320.68, 28.33) * mm, "construction": true});
            skLineSegment(sketch, "E160", {"start": v(288.93, -28.33) * mm, "end": v(320.68, -28.33) * mm, "construction": true});
            skCircle(sketch, "E161", {"center": v(304.8, 28.33) * mm, "radius": 2 * mm});
            skCircle(sketch, "E162", {"center": v(304.8, -28.33) * mm, "radius": 2 * mm});
            skPoint(sketch, "E163.visualSharp", {"position": v(315.12, 11.9) * mm});
            skArc(sketch, "E163.filletArc", {"start": v(315.12, 9.53) * mm, "mid": v(314.42, 11.2) * mm, "end": v(312.74, 11.9) * mm});
            skPoint(sketch, "E164.visualSharp", {"position": v(315.12, 7.14) * mm});
            skArc(sketch, "E164.filletArc", {"start": v(312.74, 7.14) * mm, "mid": v(314.42, 7.84) * mm, "end": v(315.12, 9.53) * mm});
            skPoint(sketch, "E165.visualSharp", {"position": v(294.48, 7.14) * mm});
            skArc(sketch, "E165.filletArc", {"start": v(294.48, 9.53) * mm, "mid": v(295.18, 7.84) * mm, "end": v(296.86, 7.14) * mm});
            skPoint(sketch, "E166.visualSharp", {"position": v(294.48, 11.9) * mm});
            skArc(sketch, "E166.filletArc", {"start": v(296.86, 11.9) * mm, "mid": v(295.18, 11.2) * mm, "end": v(294.48, 9.53) * mm});
            skLineSegment(sketch, "E167.bottom", {"start": v(315.12, 11.9) * mm, "end": v(294.48, 11.9) * mm, "construction": true});
            skLineSegment(sketch, "E167.top", {"start": v(315.12, 7.14) * mm, "end": v(294.48, 7.14) * mm, "construction": true});
            skLineSegment(sketch, "E167.left", {"start": v(315.12, 11.9) * mm, "end": v(315.12, 7.14) * mm, "construction": true});
            skLineSegment(sketch, "E167.right", {"start": v(294.48, 11.9) * mm, "end": v(294.48, 7.14) * mm, "construction": true});
            skPoint(sketch, "E168.visualSharp", {"position": v(294.48, -13.5) * mm});
            skArc(sketch, "E168.filletArc", {"start": v(296.86, -13.5) * mm, "mid": v(295.18, -14.2) * mm, "end": v(294.48, -15.88) * mm});
            skPoint(sketch, "E169.visualSharp", {"position": v(294.48, -18.26) * mm});
            skArc(sketch, "E169.filletArc", {"start": v(294.48, -15.88) * mm, "mid": v(295.18, -17.56) * mm, "end": v(296.86, -18.26) * mm});
            skPoint(sketch, "E170.visualSharp", {"position": v(315.12, -13.5) * mm});
            skArc(sketch, "E170.filletArc", {"start": v(315.12, -15.88) * mm, "mid": v(314.42, -14.2) * mm, "end": v(312.74, -13.5) * mm});
            skPoint(sketch, "E171.visualSharp", {"position": v(315.12, -18.26) * mm});
            skArc(sketch, "E171.filletArc", {"start": v(312.74, -18.26) * mm, "mid": v(314.42, -17.56) * mm, "end": v(315.12, -15.88) * mm});
            skLineSegment(sketch, "E172.bottom", {"start": v(315.12, -18.26) * mm, "end": v(294.48, -18.26) * mm, "construction": true});
            skLineSegment(sketch, "E172.top", {"start": v(315.12, -13.5) * mm, "end": v(294.48, -13.5) * mm, "construction": true});
            skLineSegment(sketch, "E172.left", {"start": v(315.12, -18.26) * mm, "end": v(315.12, -13.5) * mm, "construction": true});
            skLineSegment(sketch, "E172.right", {"start": v(294.48, -18.26) * mm, "end": v(294.48, -13.5) * mm, "construction": true});
            skSolve(sketch);
        }
        {
            var Q0;
            Q0 = qSketchRegion(id + "F10", true);
            extrude(context, id + "F11", {"entities" : qUnion([Q0]), "depth" : 2.54 * mm});
        }
    });
